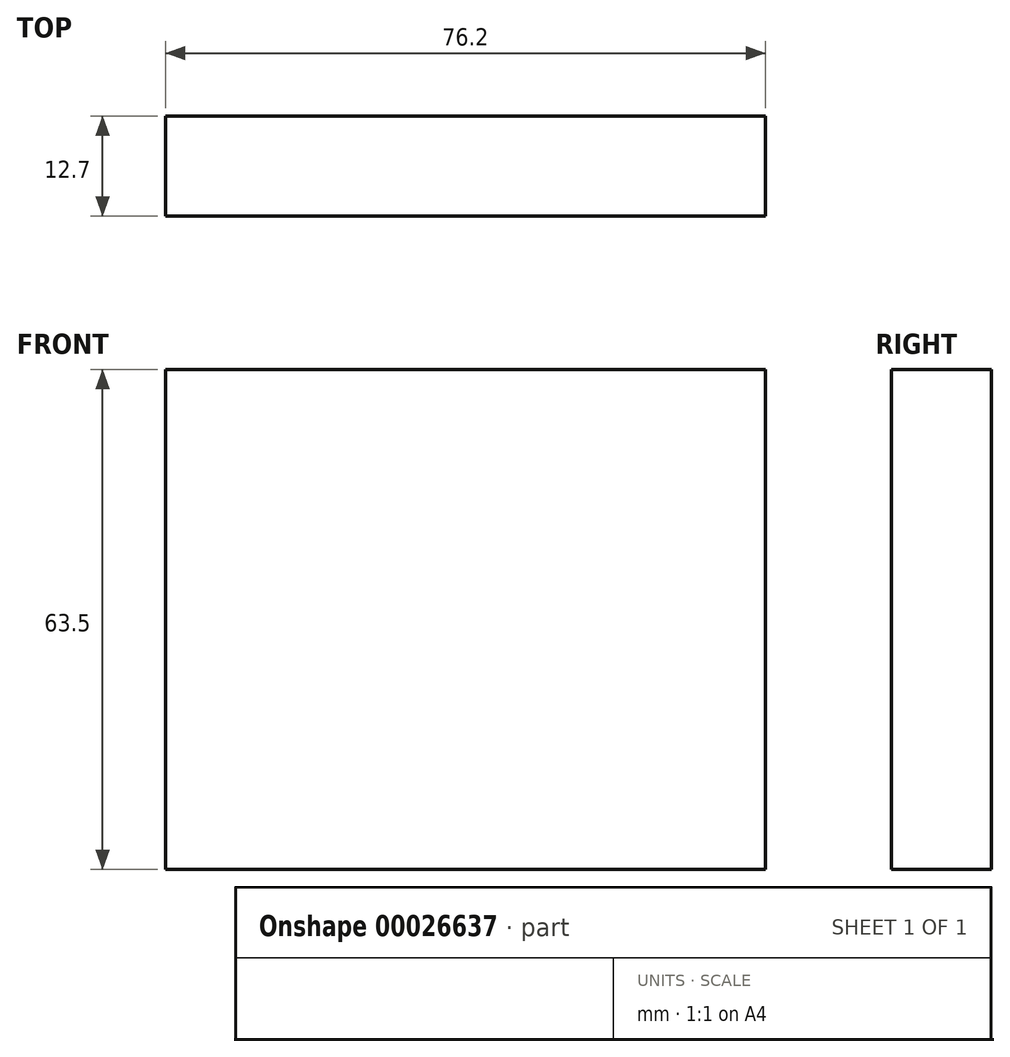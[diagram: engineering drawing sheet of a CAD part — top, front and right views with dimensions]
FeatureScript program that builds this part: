
annotation { "Feature Type Name" : "Feature", "Feature Type Description" : "" }
export const myFeature = defineFeature(function(context is Context, id is Id, definition is map)
    precondition{}
    {
        {
            var Q0;
            Q0=qCreatedBy(makeId("Front.planeOp"),FACE);
            var sketch = newSketch(context, id + "F0", { "sketchPlane" : qUnion([Q0])});
            skLineSegment(sketch, "E0.bottom", {"start": v(-58.74, 18.8) * mm, "end": v(17.46, 18.8) * mm});
            skLineSegment(sketch, "E0.top", {"start": v(-58.74, -44.7) * mm, "end": v(17.46, -44.7) * mm});
            skLineSegment(sketch, "E0.left", {"start": v(-58.74, 18.8) * mm, "end": v(-58.74, -44.7) * mm});
            skLineSegment(sketch, "E0.right", {"start": v(17.46, 18.8) * mm, "end": v(17.46, -44.7) * mm});
            skSolve(sketch);
        }
        {
            var Q0;
            Q0=makeQuery(id+"F0.imprint","IMPRINT",FACE,{"disambiguationData":[TD([[makeQuery(id+"F0.imprint","IMPRINT",EDGE,{"derivedFrom":sQuery(id+"F0.wireOp",EDGE,"E0.bottom")}),-1.0]])]});
            extrude(context, id + "F1", {"entities" : qUnion([Q0]), "depth" : 12.7 * mm});
        }
    });
